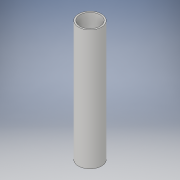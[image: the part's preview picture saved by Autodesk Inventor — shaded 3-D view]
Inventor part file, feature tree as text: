
AUTODESK INVENTOR PART (.ipt)
format: ipt  version: 2018 (Build 220112000, 112)  size: 95,232 bytes
history: native  units: in
note: dims shown in document units (in); Inventor stores cm internally (conversion verified against a paired STEP export)
features: extrude x1, sketch x1
ambient origin geometry x8: Origin, YZ Plane, XZ Plane, XY Plane, X Axis, Y Axis, Z Axis, Center Point
bodies: Solid1 (feature_tree)
feature tree (2):
  extrude  "Extrusion1"  Depth=6.0in
  sketch  "Sketch1"  dims[d0=1.15in d1=1.0in d2=6.0in d3=0.0in]
